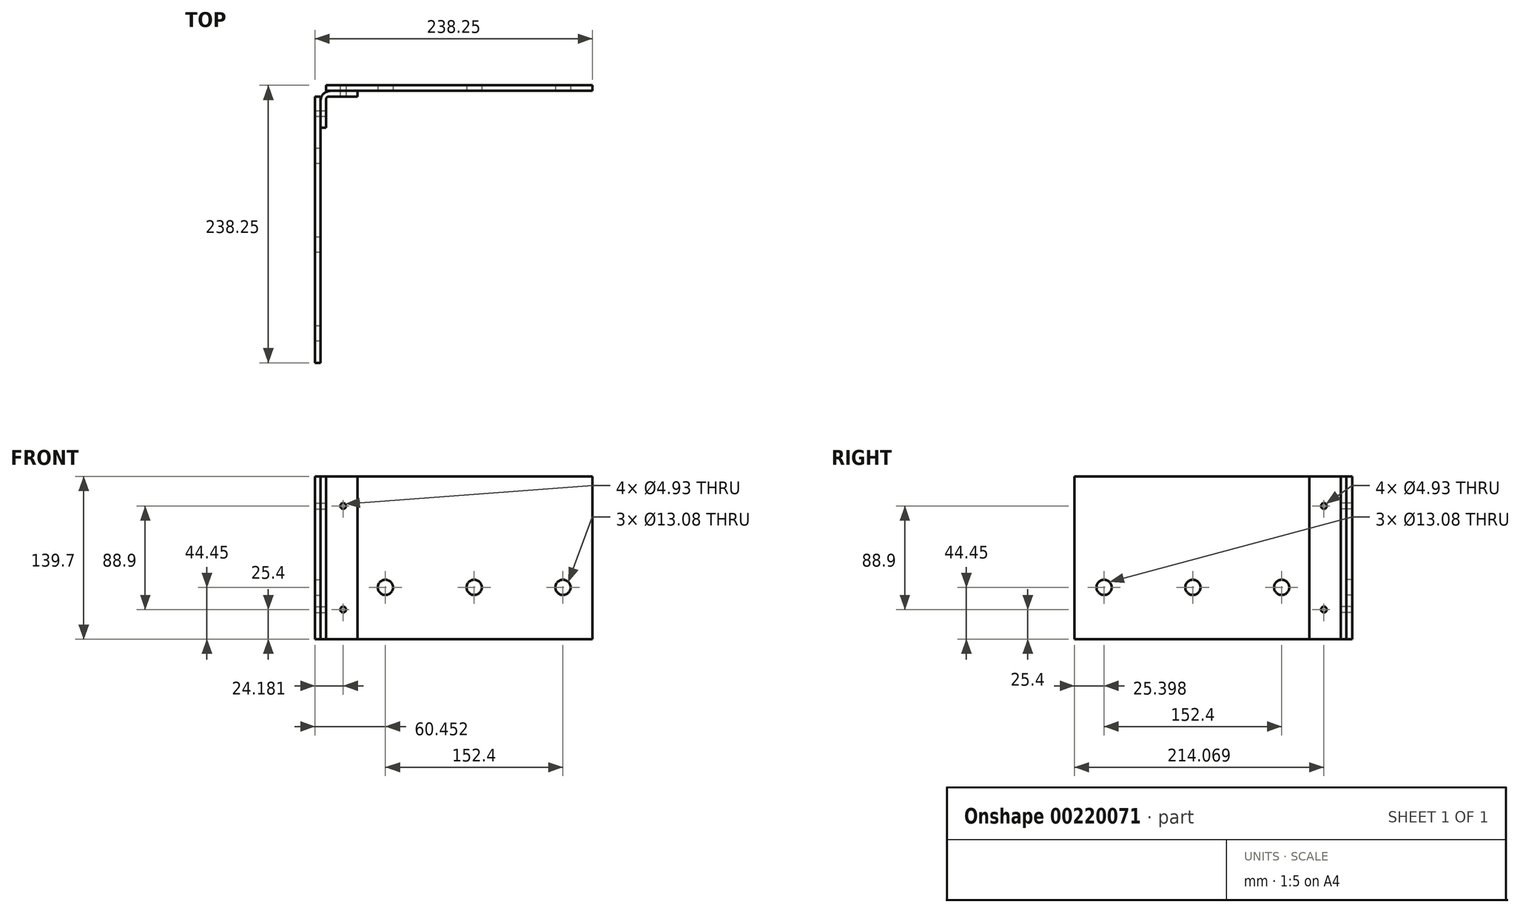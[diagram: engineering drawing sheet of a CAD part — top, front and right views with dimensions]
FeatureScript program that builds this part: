
annotation { "Feature Type Name" : "Feature", "Feature Type Description" : "" }
export const myFeature = defineFeature(function(context is Context, id is Id, definition is map)
    precondition{}
    {
        {
            var Q0;
            Q0=qCreatedBy(makeId("Top.planeOp"),FACE);
            var sketch = newSketch(context, id + "F0", { "sketchPlane" : qUnion([Q0])});
            skLineSegment(sketch, "E0", {"start": v(9.65, 0) * mm, "end": v(238.25, 0) * mm});
            skLineSegment(sketch, "E1", {"start": v(0, -9.65) * mm, "end": v(0, -238.25) * mm});
            skLineSegment(sketch, "E2", {"start": v(4.78, -9.65) * mm, "end": v(4.78, -238.25) * mm});
            skLineSegment(sketch, "E3", {"start": v(9.65, -4.78) * mm, "end": v(238.25, -4.78) * mm});
            skLineSegment(sketch, "E4", {"start": v(9.65, 16) * mm, "end": v(9.65, -9.65) * mm, "construction": true});
            skLineSegment(sketch, "E5", {"start": v(9.65, -9.65) * mm, "end": v(-10.16, -9.65) * mm, "construction": true});
            skPoint(sketch, "E6.orphan", {"position": v(0, 0) * mm});
            skLineSegment(sketch, "E7", {"start": v(9.65, 0) * mm, "end": v(9.65, -4.78) * mm});
            skLineSegment(sketch, "E8", {"start": v(0, -9.65) * mm, "end": v(4.78, -9.65) * mm});
            skLineSegment(sketch, "E9", {"start": v(238.25, 0) * mm, "end": v(238.25, -4.78) * mm});
            skLineSegment(sketch, "E10", {"start": v(0, -238.25) * mm, "end": v(4.78, -238.25) * mm});
            skSolve(sketch);
        }
        {
            var Q0;
            Q0 = qSketchRegion(id + "F0", true);
            extrude(context, id + "F1", {"entities" : qUnion([Q0]), "depth" : 139.7 * mm});
        }
        {
            var Q0;
            Q0=makeQuery(id+"F1.opExtrude","CAP_FACE",FACE,{"disambiguationData":[OSD([sQuery(id+"F0.wireOp",EDGE,"E1"),sQuery(id+"F0.wireOp",EDGE,"E2"),sQuery(id+"F0.wireOp",EDGE,"E8"),sQuery(id+"F0.wireOp",EDGE,"E10")])],"isStart":false});
            var sketch = newSketch(context, id + "F2", { "sketchPlane" : qUnion([Q0])});
            skLineSegment(sketch, "E11.0", {"start": v(4.78, -13.41) * mm, "end": v(4.78, -36.53) * mm});
            skLineSegment(sketch, "E12.0", {"start": v(13.41, -4.78) * mm, "end": v(36.53, -4.78) * mm});
            skLineSegment(sketch, "E13", {"start": v(11.84, -9.55) * mm, "end": v(36.53, -9.55) * mm});
            skLineSegment(sketch, "E14", {"start": v(9.55, -11.84) * mm, "end": v(9.55, -36.53) * mm});
            skArc(sketch, "E15.filletArc", {"start": v(11.84, -9.55) * mm, "mid": v(10.22, -10.22) * mm, "end": v(9.55, -11.84) * mm});
            skPoint(sketch, "E16.newPointA", {"position": v(4.78, -9.65) * mm});
            skPoint(sketch, "E16.newPointB", {"position": v(9.65, -4.78) * mm});
            skArc(sketch, "E16.filletArc", {"start": v(13.41, -4.78) * mm, "mid": v(7.3, -7.3) * mm, "end": v(4.78, -13.41) * mm});
            skLineSegment(sketch, "E17", {"start": v(4.78, -36.53) * mm, "end": v(9.55, -36.53) * mm});
            skLineSegment(sketch, "E18", {"start": v(36.53, -4.78) * mm, "end": v(36.53, -9.55) * mm});
            skPoint(sketch, "E19.orphan", {"position": v(4.78, -238.25) * mm});
            skPoint(sketch, "E20.orphan", {"position": v(238.25, -4.78) * mm});
            skSolve(sketch);
        }
        {
            var Q0;
            Q0 = qSketchRegion(id + "F2", true);
            extrude(context, id + "F3", {"entities" : qUnion([Q0]), "oppositeDirection" : true, "depth" : 139.7 * mm});
        }
        {
            var Q0;
            Q0=makeQuery(id+"F1.opExtrude","SWEPT_FACE",FACE,{"disambiguationData":[OSD([sQuery(id+"F0.wireOp",EDGE,"E2")])]});
            var sketch = newSketch(context, id + "F4", { "sketchPlane" : qUnion([Q0])});
            skLineSegment(sketch, "E21", {"start": v(-236.89, 44.45) * mm, "end": v(-40.15, 44.45) * mm, "construction": true});
            skCircle(sketch, "E22", {"center": v(-212.85, 44.45) * mm, "radius": 6.54 * mm});
            skCircle(sketch, "E23", {"center": v(-136.65, 44.45) * mm, "radius": 6.54 * mm});
            skCircle(sketch, "E24", {"center": v(-60.45, 44.45) * mm, "radius": 6.54 * mm});
            skSolve(sketch);
        }
        {
            var Q0;
            Q0 = qSketchRegion(id + "F4", true);
            extrude(context, id + "F5", {"entities" : qUnion([Q0]), "operationType" : NewBodyOperationType.REMOVE, "oppositeDirection" : true, "depth" : 25.4 * mm});
        }
        {
            var Q0;
            Q0=makeQuery(id+"F1.opExtrude","SWEPT_FACE",FACE,{"disambiguationData":[OSD([sQuery(id+"F0.wireOp",EDGE,"E3")])]});
            var sketch = newSketch(context, id + "F6", { "sketchPlane" : qUnion([Q0])});
            skLineSegment(sketch, "E25", {"start": v(50.88, 44.45) * mm, "end": v(252.2, 44.45) * mm, "construction": true});
            skCircle(sketch, "E26", {"center": v(212.85, 44.45) * mm, "radius": 6.54 * mm});
            skCircle(sketch, "E27", {"center": v(136.65, 44.45) * mm, "radius": 6.54 * mm});
            skCircle(sketch, "E28", {"center": v(60.45, 44.45) * mm, "radius": 6.54 * mm});
            skSolve(sketch);
        }
        {
            var Q0;
            Q0 = qSketchRegion(id + "F6", true);
            extrude(context, id + "F7", {"entities" : qUnion([Q0]), "operationType" : NewBodyOperationType.REMOVE, "oppositeDirection" : true, "depth" : 25.4 * mm});
        }
        {
            var Q0;
            Q0=makeQuery(id+"F3.opExtrude","SWEPT_FACE",FACE,{"disambiguationData":[OSD([sQuery(id+"F2.wireOp",EDGE,"E14")])]});
            var sketch = newSketch(context, id + "F8", { "sketchPlane" : qUnion([Q0])});
            skLineSegment(sketch, "E29", {"start": v(-24.18, 204.91) * mm, "end": v(-24.18, -62.9) * mm, "construction": true});
            skCircle(sketch, "E30", {"center": v(-24.18, 114.3) * mm, "radius": 2.46 * mm});
            skCircle(sketch, "E31", {"center": v(-24.18, 25.4) * mm, "radius": 2.46 * mm});
            skSolve(sketch);
        }
        {
            var Q0;
            Q0 = qSketchRegion(id + "F8", true);
            extrude(context, id + "F9", {"entities" : qUnion([Q0]), "operationType" : NewBodyOperationType.REMOVE, "oppositeDirection" : true, "depth" : 25.4 * mm});
        }
        {
            var Q0;
            Q0=makeQuery(id+"F3.opExtrude","SWEPT_FACE",FACE,{"disambiguationData":[OSD([sQuery(id+"F2.wireOp",EDGE,"E13")])]});
            var sketch = newSketch(context, id + "F10", { "sketchPlane" : qUnion([Q0])});
            skLineSegment(sketch, "E32", {"start": v(24.18, 197.76) * mm, "end": v(24.18, -60.95) * mm, "construction": true});
            skCircle(sketch, "E33", {"center": v(24.18, 114.3) * mm, "radius": 2.46 * mm});
            skCircle(sketch, "E34", {"center": v(24.18, 25.4) * mm, "radius": 2.46 * mm});
            skSolve(sketch);
        }
        {
            var Q0;
            Q0 = qSketchRegion(id + "F10", true);
            extrude(context, id + "F11", {"entities" : qUnion([Q0]), "operationType" : NewBodyOperationType.REMOVE, "oppositeDirection" : true, "depth" : 25.4 * mm});
        }
        {
            var Q0;
            Q0=makeQuery(id+"F1.opExtrude","SWEPT_FACE",FACE,{"disambiguationData":[OSD([sQuery(id+"F0.wireOp",EDGE,"E2")])]});
            var sketch = newSketch(context, id + "F12", { "sketchPlane" : qUnion([Q0])});
            skCircle(sketch, "E35.0", {"center": v(-24.18, 114.3) * mm, "radius": 2.46 * mm});
            skCircle(sketch, "E36.0", {"center": v(-24.18, 25.4) * mm, "radius": 2.46 * mm});
            skSolve(sketch);
        }
        {
            var Q0;
            Q0 = qSketchRegion(id + "F12", true);
            extrude(context, id + "F13", {"entities" : qUnion([Q0]), "operationType" : NewBodyOperationType.REMOVE, "oppositeDirection" : true, "depth" : 25.4 * mm});
        }
        {
            var Q0;
            Q0=makeQuery(id+"F1.opExtrude","SWEPT_FACE",FACE,{"disambiguationData":[OSD([sQuery(id+"F0.wireOp",EDGE,"E3")])]});
            var sketch = newSketch(context, id + "F14", { "sketchPlane" : qUnion([Q0])});
            skCircle(sketch, "E37.0", {"center": v(24.18, 114.3) * mm, "radius": 2.46 * mm});
            skCircle(sketch, "E38.0", {"center": v(24.18, 25.4) * mm, "radius": 2.46 * mm});
            skSolve(sketch);
        }
        {
            var Q0;
            Q0 = qSketchRegion(id + "F14", true);
            extrude(context, id + "F15", {"entities" : qUnion([Q0]), "operationType" : NewBodyOperationType.REMOVE, "oppositeDirection" : true, "depth" : 25.4 * mm});
        }
    });
